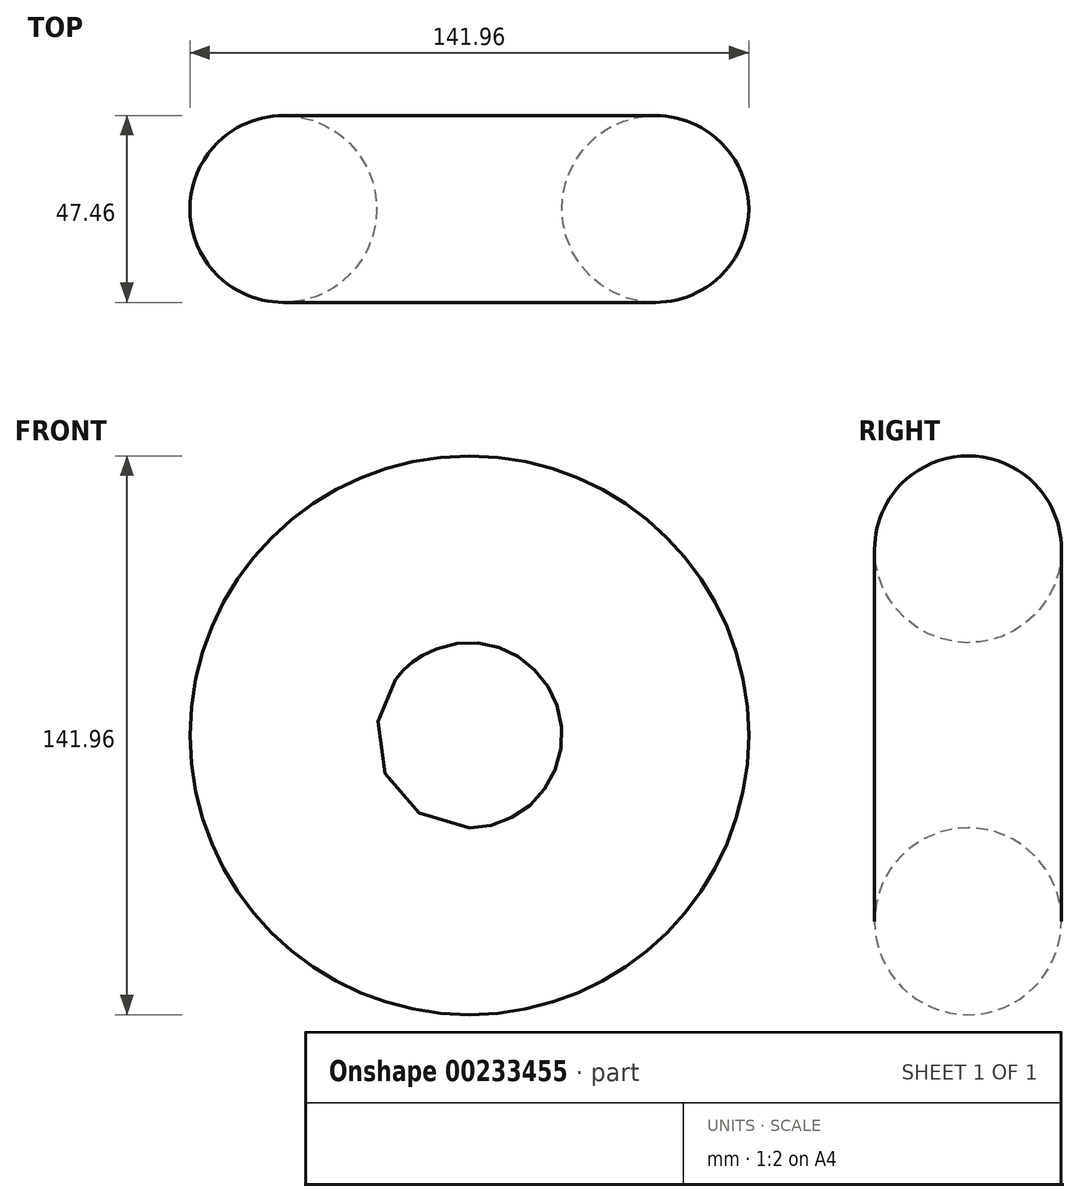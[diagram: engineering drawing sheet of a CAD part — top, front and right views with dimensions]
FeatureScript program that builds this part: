
annotation { "Feature Type Name" : "Feature", "Feature Type Description" : "" }
export const myFeature = defineFeature(function(context is Context, id is Id, definition is map)
    precondition{}
    {
        {
            var Q0;
            Q0=qCreatedBy(makeId("Top.planeOp"),FACE);
            var sketch = newSketch(context, id + "F0", { "sketchPlane" : qUnion([Q0])});
            skCircle(sketch, "E0", {"center": v(0, 0) * mm, "radius": 23.73 * mm});
            skSolve(sketch);
        }
        {
            var Q0;
            Q0=qCreatedBy(makeId("Front.planeOp"),FACE);
            var sketch = newSketch(context, id + "F1", { "sketchPlane" : qUnion([Q0])});
            skCircle(sketch, "E1", {"center": v(47.25, 0) * mm, "radius": 47.38 * mm});
            skSolve(sketch);
        }
        {
            var Q0;
            Q0=makeQuery(id+"F0.imprint","IMPRINT",FACE,{"disambiguationData":[TD([[makeQuery(id+"F0.imprint","IMPRINT",EDGE,{"derivedFrom":sQuery(id+"F0.wireOp",EDGE,"E0")}),1.0]])]});
            var Q1;
            Q1=sQuery(id+"F1.wireOp",EDGE,"E1");
            sweep(context, id + "F2", {"profiles" : qUnion([Q0]), "path" : qUnion([Q1])});
        }
    });
